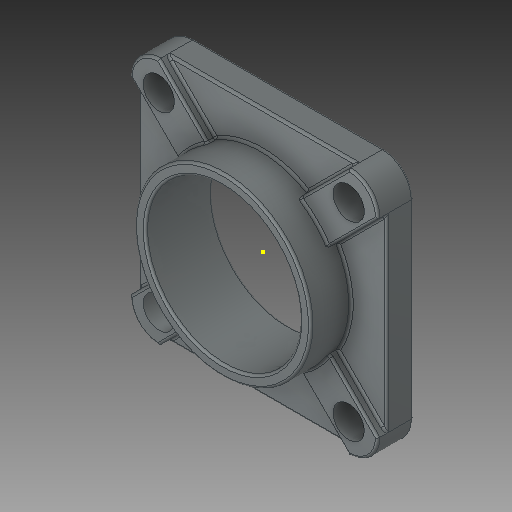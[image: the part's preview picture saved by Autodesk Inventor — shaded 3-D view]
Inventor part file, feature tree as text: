
AUTODESK INVENTOR PART (.ipt)
format: ipt  version: 2019 (Build 230136000, 136)  size: 484,864 bytes
history: native  units: in
note: dims shown in document units (in); Inventor stores cm internally (conversion verified against a paired STEP export)
features: sketch x10, other x3
ambient origin geometry x8: Origin, YZ Plane, XZ Plane, XY Plane, X Axis, Y Axis, Z Axis, Center Point
bodies: Solid1 (feature_tree)
feature tree (13):
  other  "project flange bearing part1_MIR1.ipt"
  other  "Solid1::project flange bearing part1_MIR1.ipt"
  other  "TaggingFeature1"
  sketch  "Sketch1"  dims[d0=0.3937in]
  sketch  "Sketch2"
  sketch  "Sketch3"
  sketch  "Sketch4"
  sketch  "Sketch5"
  sketch  "Sketch6"
  sketch  "Sketch7"
  sketch  "Sketch8"
  sketch  "Sketch9"
  sketch  "Sketch10"
